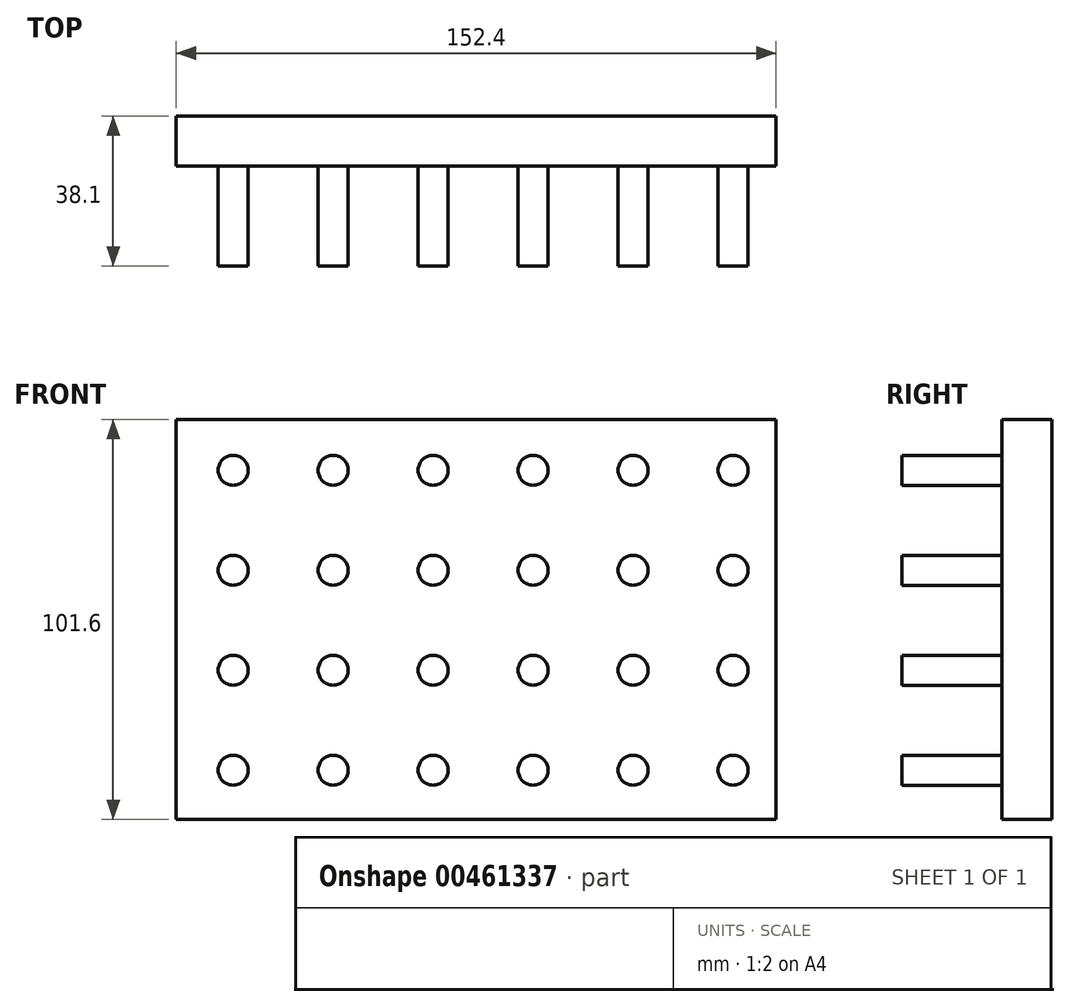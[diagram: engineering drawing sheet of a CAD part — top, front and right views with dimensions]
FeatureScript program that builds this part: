
annotation { "Feature Type Name" : "Feature", "Feature Type Description" : "" }
export const myFeature = defineFeature(function(context is Context, id is Id, definition is map)
    precondition{}
    {
        {
            var Q0;
            Q0=qCreatedBy(makeId("Front.planeOp"),FACE);
            var sketch = newSketch(context, id + "F0", { "sketchPlane" : qUnion([Q0])});
            skLineSegment(sketch, "E0.bottom", {"start": v(0, 0) * mm, "end": v(152.4, 0) * mm});
            skLineSegment(sketch, "E0.top", {"start": v(0, 101.6) * mm, "end": v(152.4, 101.6) * mm});
            skLineSegment(sketch, "E0.left", {"start": v(0, 0) * mm, "end": v(0, 101.6) * mm});
            skLineSegment(sketch, "E0.right", {"start": v(152.4, 0) * mm, "end": v(152.4, 101.6) * mm});
            skSolve(sketch);
        }
        {
            var Q0;
            Q0=makeQuery(id+"F0.imprint","IMPRINT",FACE,{"disambiguationData":[TD([[makeQuery(id+"F0.imprint","IMPRINT",EDGE,{"derivedFrom":sQuery(id+"F0.wireOp",EDGE,"E0.bottom")}),1.0]])]});
            var Q1;
            Q1=makeQuery(id+"F0.imprint","IMPRINT",FACE,{"disambiguationData":[TD([[makeQuery(id+"F0.imprint","IMPRINT",EDGE,{"derivedFrom":sQuery(id+"F0.wireOp",EDGE,"pHg4IFhl-gMKX-qdAc-06Zq-nsIRwmyl1yAR")}),1.0]])]});
            extrude(context, id + "F1", {"entities" : qUnion([Q0, Q1]), "depth" : 12.7 * mm});
        }
        {
            var Q0;
            Q0=makeQuery(id+"F1.opExtrude","CAP_FACE",FACE,{"disambiguationData":[OSD([sQuery(id+"F0.wireOp",EDGE,"E0.bottom"),sQuery(id+"F0.wireOp",EDGE,"E0.top"),sQuery(id+"F0.wireOp",EDGE,"E0.left"),sQuery(id+"F0.wireOp",EDGE,"E0.right")])],"isStart":false});
            var sketch = newSketch(context, id + "F2", { "sketchPlane" : qUnion([Q0])});
            skCircle(sketch, "E1", {"center": v(14.48, 12.51) * mm, "radius": 3.81 * mm});
            skCircle(sketch, "E2.0.1.0", {"center": v(14.48, 37.91) * mm, "radius": 3.81 * mm});
            skCircle(sketch, "E2.0.2.0", {"center": v(14.48, 63.31) * mm, "radius": 3.81 * mm});
            skCircle(sketch, "E2.0.3.0", {"center": v(14.48, 88.71) * mm, "radius": 3.81 * mm});
            skCircle(sketch, "E2.1.0.0", {"center": v(39.88, 12.51) * mm, "radius": 3.81 * mm});
            skCircle(sketch, "E2.1.1.0", {"center": v(39.88, 37.91) * mm, "radius": 3.81 * mm});
            skCircle(sketch, "E2.1.2.0", {"center": v(39.88, 63.31) * mm, "radius": 3.81 * mm});
            skCircle(sketch, "E2.1.3.0", {"center": v(39.88, 88.71) * mm, "radius": 3.81 * mm});
            skCircle(sketch, "E2.2.0.0", {"center": v(65.28, 12.51) * mm, "radius": 3.81 * mm});
            skCircle(sketch, "E2.2.1.0", {"center": v(65.28, 37.91) * mm, "radius": 3.81 * mm});
            skCircle(sketch, "E2.2.2.0", {"center": v(65.28, 63.31) * mm, "radius": 3.81 * mm});
            skCircle(sketch, "E2.2.3.0", {"center": v(65.28, 88.71) * mm, "radius": 3.81 * mm});
            skCircle(sketch, "E2.3.0.0", {"center": v(90.68, 12.51) * mm, "radius": 3.81 * mm});
            skCircle(sketch, "E2.3.1.0", {"center": v(90.68, 37.91) * mm, "radius": 3.81 * mm});
            skCircle(sketch, "E2.3.2.0", {"center": v(90.68, 63.31) * mm, "radius": 3.81 * mm});
            skCircle(sketch, "E2.3.3.0", {"center": v(90.68, 88.71) * mm, "radius": 3.81 * mm});
            skCircle(sketch, "E2.4.0.0", {"center": v(116.08, 12.51) * mm, "radius": 3.81 * mm});
            skCircle(sketch, "E2.4.1.0", {"center": v(116.08, 37.91) * mm, "radius": 3.81 * mm});
            skCircle(sketch, "E2.4.2.0", {"center": v(116.08, 63.31) * mm, "radius": 3.81 * mm});
            skCircle(sketch, "E2.4.3.0", {"center": v(116.08, 88.71) * mm, "radius": 3.81 * mm});
            skCircle(sketch, "E2.5.0.0", {"center": v(141.48, 12.51) * mm, "radius": 3.81 * mm});
            skCircle(sketch, "E2.5.1.0", {"center": v(141.48, 37.91) * mm, "radius": 3.81 * mm});
            skCircle(sketch, "E2.5.2.0", {"center": v(141.48, 63.31) * mm, "radius": 3.81 * mm});
            skCircle(sketch, "E2.5.3.0", {"center": v(141.48, 88.71) * mm, "radius": 3.81 * mm});
            skLineSegment(sketch, "E2.direction1", {"start": v(14.48, 12.51) * mm, "end": v(39.88, 12.51) * mm, "construction": true});
            skLineSegment(sketch, "E2.direction2", {"start": v(14.48, 12.51) * mm, "end": v(14.48, 37.91) * mm, "construction": true});
            skSolve(sketch);
        }
        {
            var Q0;
            Q0 = qSketchRegion(id + "F2", true);
            extrude(context, id + "F3", {"entities" : qUnion([Q0]), "operationType" : NewBodyOperationType.ADD, "depth" : 25.4 * mm});
        }
    });
